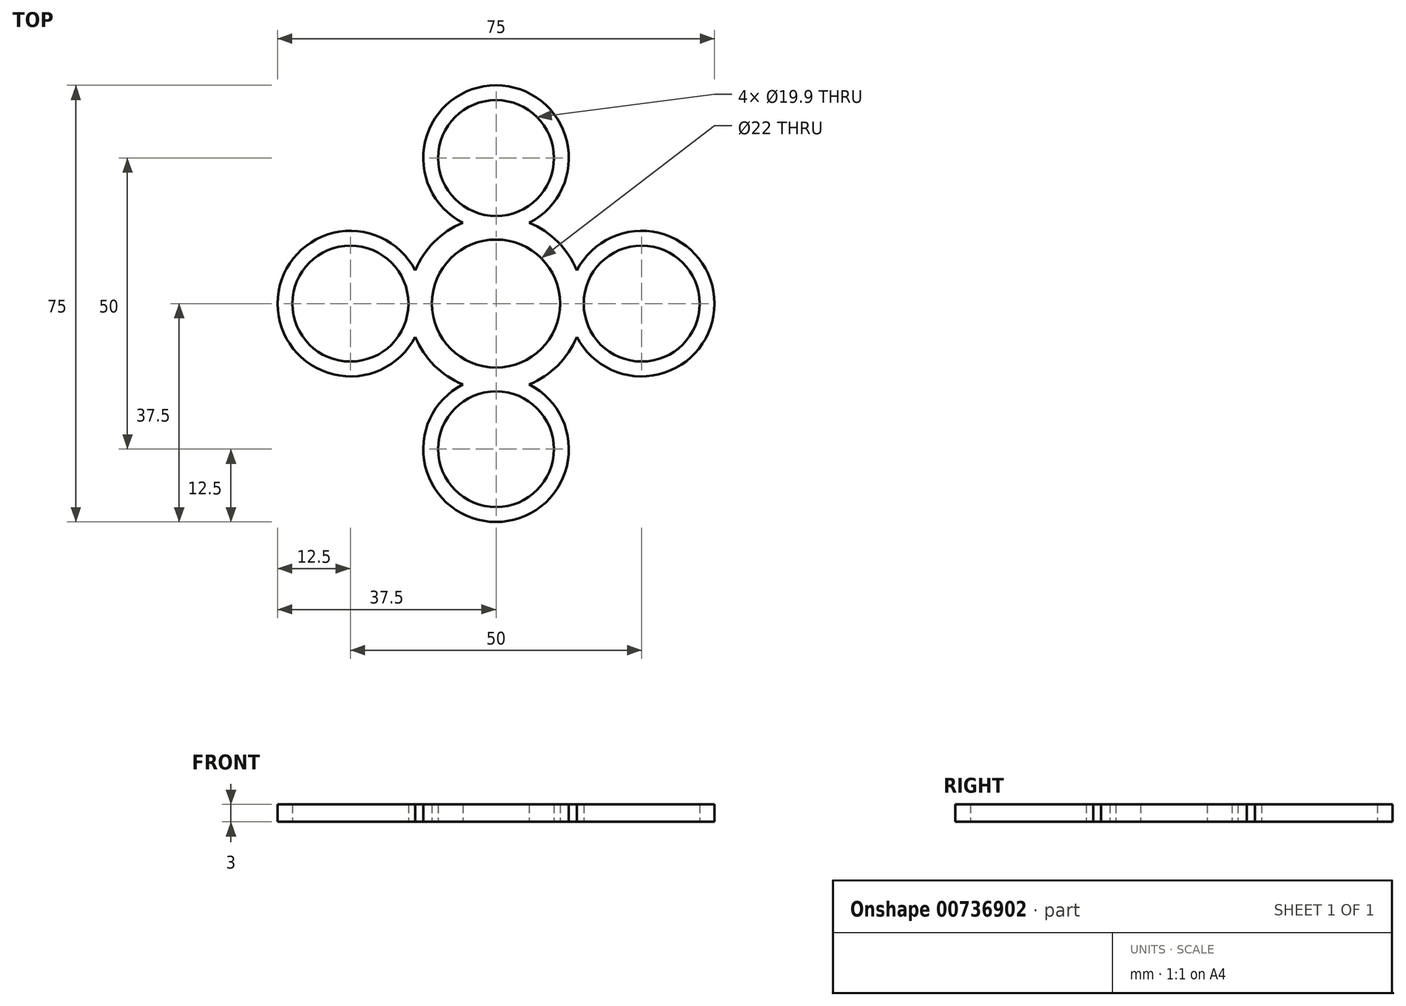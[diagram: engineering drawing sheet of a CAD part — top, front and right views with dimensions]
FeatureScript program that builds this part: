
annotation { "Feature Type Name" : "Feature", "Feature Type Description" : "" }
export const myFeature = defineFeature(function(context is Context, id is Id, definition is map)
    precondition{}
    {
        {
            var Q0;
            Q0=qCreatedBy(makeId("Top.planeOp"),FACE);
            var sketch = newSketch(context, id + "F0", { "sketchPlane" : qUnion([Q0])});
            skArc(sketch, "E0", {"start": v(7.78, 7.78) * mm, "mid": v(0, 11) * mm, "end": v(-7.78, 7.78) * mm});
            skCircle(sketch, "E1", {"center": v(0, 25) * mm, "radius": 9.95 * mm});
            skArc(sketch, "E2", {"start": v(-5.7, 13.87) * mm, "mid": v(-8.32, 12.48) * mm, "end": v(-10.6, 10.6) * mm});
            skArc(sketch, "E3", {"start": v(5.7, 13.88) * mm, "mid": v(0, 37.5) * mm, "end": v(-5.7, 13.88) * mm});
            skArc(sketch, "E4.trimOffspring", {"start": v(10.6, 10.6) * mm, "mid": v(8.32, 12.48) * mm, "end": v(5.7, 13.87) * mm});
            skArc(sketch, "E5.1.0", {"start": v(-13.88, 5.7) * mm, "mid": v(-37.5, 0) * mm, "end": v(-13.88, -5.7) * mm});
            skArc(sketch, "E5.1.1", {"start": v(-7.78, 7.78) * mm, "mid": v(-11, 0) * mm, "end": v(-7.78, -7.78) * mm});
            skArc(sketch, "E5.1.2", {"start": v(-10.6, 10.6) * mm, "mid": v(-12.48, 8.32) * mm, "end": v(-13.87, 5.7) * mm});
            skArc(sketch, "E5.1.3", {"start": v(-13.87, -5.7) * mm, "mid": v(-12.48, -8.32) * mm, "end": v(-10.6, -10.6) * mm});
            skCircle(sketch, "E5.1.4", {"center": v(-25, 0) * mm, "radius": 9.95 * mm});
            skArc(sketch, "E5.2.0", {"start": v(-5.7, -13.88) * mm, "mid": v(0, -37.5) * mm, "end": v(5.7, -13.88) * mm});
            skArc(sketch, "E5.2.1", {"start": v(-7.78, -7.78) * mm, "mid": v(0, -11) * mm, "end": v(7.78, -7.78) * mm});
            skArc(sketch, "E5.2.2", {"start": v(-10.6, -10.6) * mm, "mid": v(-8.32, -12.48) * mm, "end": v(-5.7, -13.87) * mm});
            skArc(sketch, "E5.2.3", {"start": v(5.7, -13.87) * mm, "mid": v(8.32, -12.48) * mm, "end": v(10.6, -10.6) * mm});
            skCircle(sketch, "E5.2.4", {"center": v(0, -25) * mm, "radius": 9.95 * mm});
            skArc(sketch, "E5.3.0", {"start": v(13.88, -5.7) * mm, "mid": v(37.5, 0) * mm, "end": v(13.88, 5.7) * mm});
            skArc(sketch, "E5.3.1", {"start": v(7.78, -7.78) * mm, "mid": v(11, 0) * mm, "end": v(7.78, 7.78) * mm});
            skArc(sketch, "E5.3.2", {"start": v(10.6, -10.6) * mm, "mid": v(12.48, -8.32) * mm, "end": v(13.87, -5.7) * mm});
            skArc(sketch, "E5.3.3", {"start": v(13.87, 5.7) * mm, "mid": v(12.48, 8.32) * mm, "end": v(10.6, 10.6) * mm});
            skCircle(sketch, "E5.3.4", {"center": v(25, 0) * mm, "radius": 9.95 * mm});
            skSolve(sketch);
        }
        {
            var Q0;
            Q0 = qSketchRegion(id + "F0", true);
            extrude(context, id + "F1", {"entities" : qUnion([Q0]), "depth" : 3 * mm, "offsetDistance" : 25 * mm});
        }
    });
